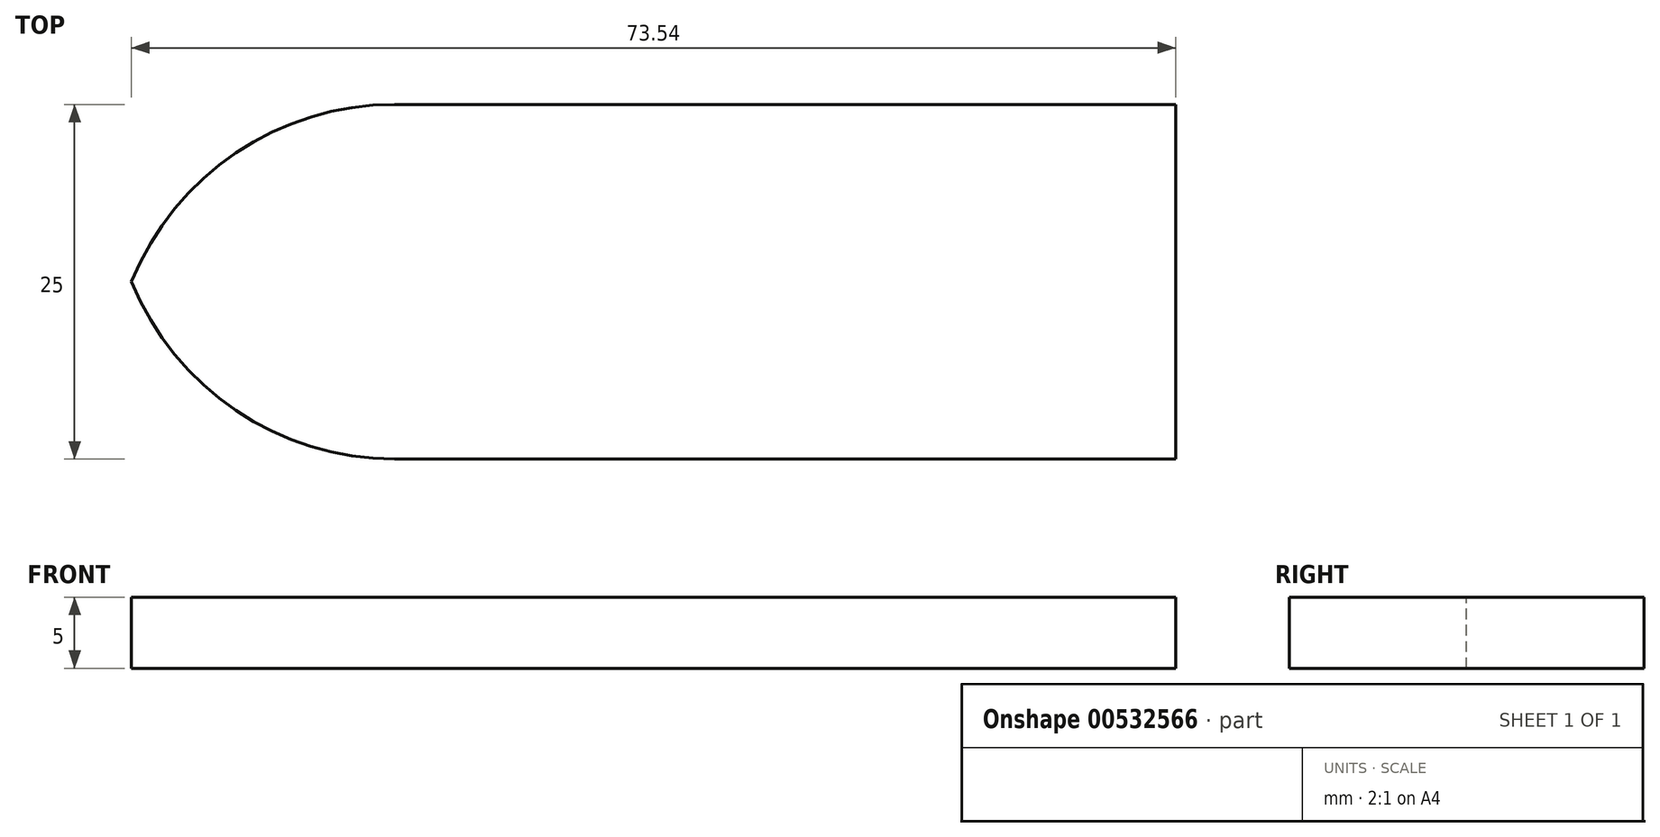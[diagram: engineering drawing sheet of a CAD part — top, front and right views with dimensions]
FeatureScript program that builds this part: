
annotation { "Feature Type Name" : "Feature", "Feature Type Description" : "" }
export const myFeature = defineFeature(function(context is Context, id is Id, definition is map)
    precondition{}
    {
        {
            var Q0;
            Q0=qCreatedBy(makeId("Top.planeOp"),FACE);
            var sketch = newSketch(context, id + "F0", { "sketchPlane" : qUnion([Q0])});
            skLineSegment(sketch, "E0.bottom", {"start": v(-37.5, 12.5) * mm, "end": v(37.5, 12.5) * mm});
            skLineSegment(sketch, "E0.top", {"start": v(-37.5, -12.5) * mm, "end": v(37.5, -12.5) * mm});
            skLineSegment(sketch, "E0.left", {"start": v(-37.5, 12.5) * mm, "end": v(-37.5, -12.5) * mm});
            skLineSegment(sketch, "E0.right", {"start": v(37.5, 12.5) * mm, "end": v(37.5, -12.5) * mm});
            skPoint(sketch, "E0.middle", {"position": v(0, 0) * mm});
            skSolve(sketch);
        }
        {
            var Q0;
            Q0=makeQuery(id+"F0.imprint","IMPRINT",FACE,{"disambiguationData":[TD([[makeQuery(id+"F0.imprint","IMPRINT",EDGE,{"derivedFrom":sQuery(id+"F0.wireOp",EDGE,"E0.bottom")}),-1.0]])]});
            extrude(context, id + "F1", {"entities" : qUnion([Q0]), "depth" : 5 * mm, "offsetDistance" : 25 * mm});
        }
        {
            var Q0;
            Q0=makeQuery(id+"F1.opExtrude","SWEPT_EDGE",EDGE,{"disambiguationData":[OSD([sQuery(id+"F0.wireOp",EDGE,"E0.bottom"),sQuery(id+"F0.wireOp",EDGE,"E0.left")])]});
            var Q1;
            Q1=makeQuery(id+"F1.opExtrude","SWEPT_EDGE",EDGE,{"disambiguationData":[OSD([sQuery(id+"F0.wireOp",EDGE,"E0.top"),sQuery(id+"F0.wireOp",EDGE,"E0.left")])]});
            fillet(context, id + "F2", {"entities" : qUnion([Q0, Q1]), "radius" : 20 * mm, "tangentPropagation" : true, "allowEdgeOverflow" : false});
        }
    });
